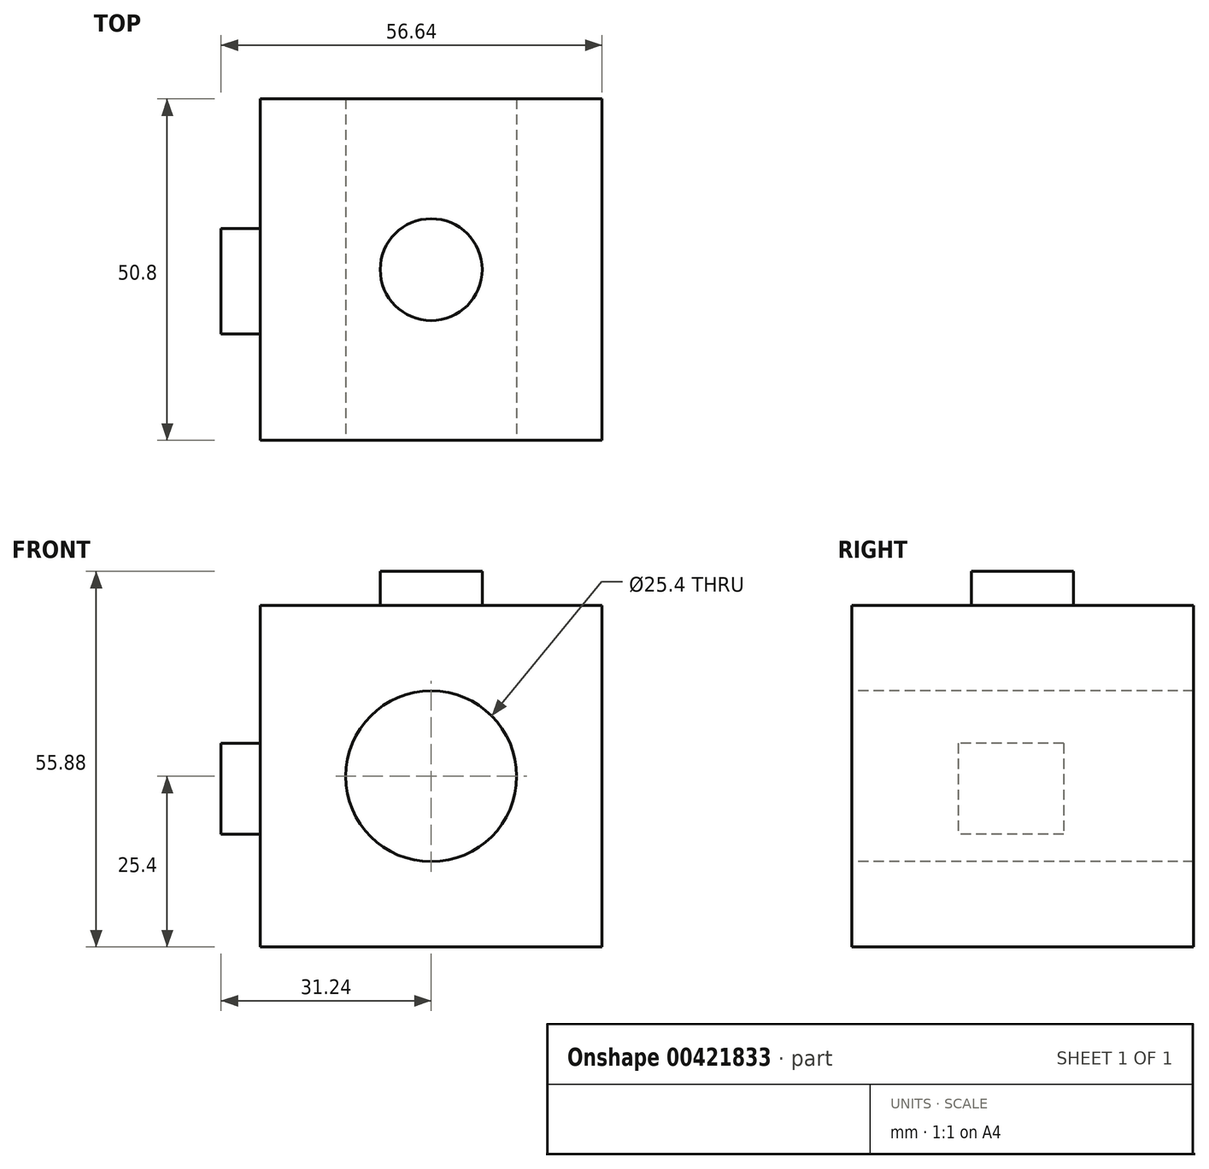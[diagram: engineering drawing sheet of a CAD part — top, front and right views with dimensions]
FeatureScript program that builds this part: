
annotation { "Feature Type Name" : "Feature", "Feature Type Description" : "" }
export const myFeature = defineFeature(function(context is Context, id is Id, definition is map)
    precondition{}
    {
        {
            var Q0;
            Q0=qCreatedBy(makeId("Front.planeOp"),FACE);
            var sketch = newSketch(context, id + "F0", { "sketchPlane" : qUnion([Q0])});
            skLineSegment(sketch, "E0.bottom", {"start": v(0, 0) * mm, "end": v(-50.8, 0) * mm});
            skLineSegment(sketch, "E0.top", {"start": v(0, 50.8) * mm, "end": v(-50.8, 50.8) * mm});
            skLineSegment(sketch, "E0.left", {"start": v(0, 0) * mm, "end": v(0, 50.8) * mm});
            skLineSegment(sketch, "E0.right", {"start": v(-50.8, 0) * mm, "end": v(-50.8, 50.8) * mm});
            skSolve(sketch);
        }
        {
            var Q0;
            Q0 = qSketchRegion(id + "F0", true);
            extrude(context, id + "F1", {"entities" : qUnion([Q0]), "depth" : 50.8 * mm});
        }
        {
            var Q0;
            Q0=makeQuery(id+"F1.opExtrude","CAP_FACE",FACE,{"disambiguationData":[OSD([sQuery(id+"F0.wireOp",EDGE,"E0.bottom"),sQuery(id+"F0.wireOp",EDGE,"E0.top"),sQuery(id+"F0.wireOp",EDGE,"E0.left"),sQuery(id+"F0.wireOp",EDGE,"E0.right")])],"isStart":false});
            var sketch = newSketch(context, id + "F2", { "sketchPlane" : qUnion([Q0])});
            skCircle(sketch, "E1", {"center": v(-25.4, 25.4) * mm, "radius": 12.7 * mm});
            skSolve(sketch);
        }
        {
            var Q0;
            Q0=makeQuery(id+"F2.imprint","IMPRINT",FACE,{"disambiguationData":[TD([[makeQuery(id+"F2.imprint","IMPRINT",EDGE,{"derivedFrom":sQuery(id+"F2.wireOp",EDGE,"E1")}),1.0]])]});
            extrude(context, id + "F3", {"entities" : qUnion([Q0]), "operationType" : NewBodyOperationType.REMOVE, "oppositeDirection" : true, "depth" : 50.8 * mm});
        }
        {
            var Q0;
            Q0=makeQuery(id+"F1.opExtrude","SWEPT_FACE",FACE,{"disambiguationData":[OSD([sQuery(id+"F0.wireOp",EDGE,"E0.right")])]});
            var sketch = newSketch(context, id + "F4", { "sketchPlane" : qUnion([Q0])});
            skLineSegment(sketch, "E2.bottom", {"start": v(19.28, 30.31) * mm, "end": v(34.98, 30.31) * mm});
            skLineSegment(sketch, "E2.top", {"start": v(19.28, 16.8) * mm, "end": v(34.98, 16.8) * mm});
            skLineSegment(sketch, "E2.left", {"start": v(19.28, 30.31) * mm, "end": v(19.28, 16.8) * mm});
            skLineSegment(sketch, "E2.right", {"start": v(34.98, 30.31) * mm, "end": v(34.98, 16.8) * mm});
            skSolve(sketch);
        }
        {
            var Q0;
            Q0=makeQuery(id+"F4.imprint","IMPRINT",FACE,{"disambiguationData":[TD([[makeQuery(id+"F4.imprint","IMPRINT",EDGE,{"derivedFrom":sQuery(id+"F4.wireOp",EDGE,"E2.bottom")}),-1.0]])]});
            extrude(context, id + "F5", {"entities" : qUnion([Q0]), "operationType" : NewBodyOperationType.ADD, "depth" : 5.84 * mm});
        }
        {
            var Q0;
            Q0=makeQuery(id+"F1.opExtrude","SWEPT_FACE",FACE,{"disambiguationData":[OSD([sQuery(id+"F0.wireOp",EDGE,"E0.top")])]});
            var sketch = newSketch(context, id + "F6", { "sketchPlane" : qUnion([Q0])});
            skCircle(sketch, "E3", {"center": v(-25.4, -25.4) * mm, "radius": 7.58 * mm});
            skSolve(sketch);
        }
        {
            var Q0;
            Q0=makeQuery(id+"F6.imprint","IMPRINT",FACE,{"disambiguationData":[TD([[makeQuery(id+"F6.imprint","IMPRINT",EDGE,{"derivedFrom":sQuery(id+"F6.wireOp",EDGE,"E3")}),1.0]])]});
            extrude(context, id + "F7", {"entities" : qUnion([Q0]), "operationType" : NewBodyOperationType.ADD, "depth" : 5.08 * mm});
        }
    });
